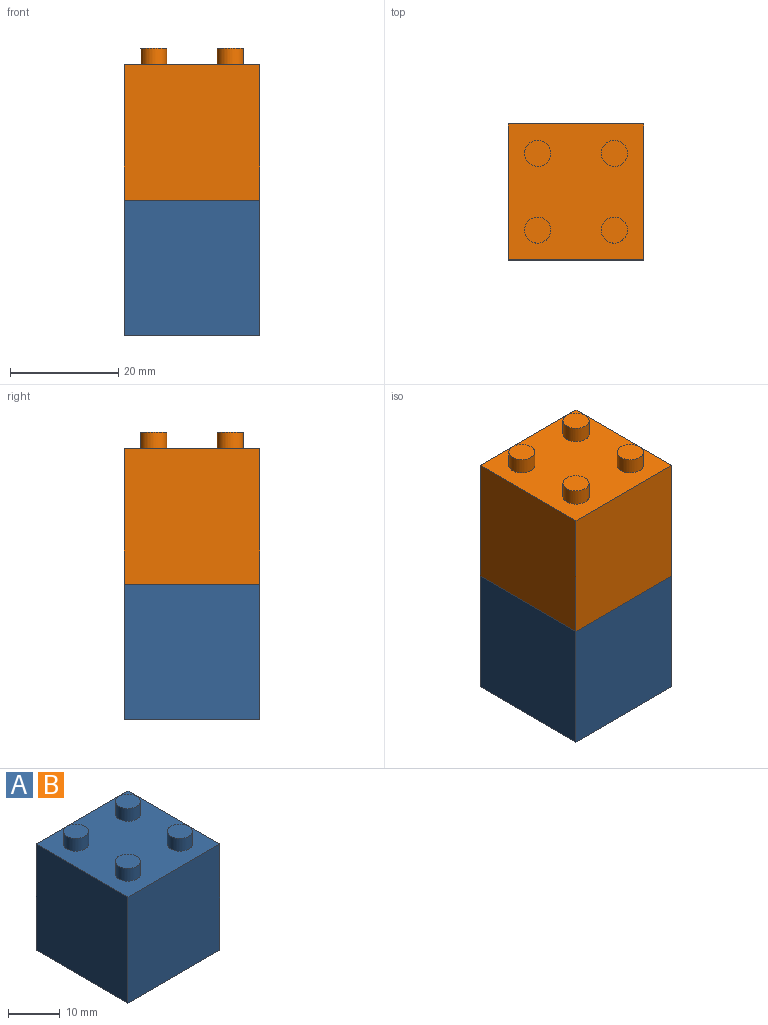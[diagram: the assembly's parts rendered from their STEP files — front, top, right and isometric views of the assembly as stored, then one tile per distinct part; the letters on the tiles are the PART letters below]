
ASSEMBLY  parts=2 mates=1
PART A: 23 faces, bbox 25x25x28 mm
  f0: plane 25x25mm, normal (0,0,-1), area 264mm2, adj f1,f2,f3,f4,f14,f15,f16,f17
  f1: plane 25x25mm, normal (1,0,0), area 625mm2, adj f0,f2,f4,f5
  f2: plane 25x25mm, normal (0,1,0), area 625mm2, adj f0,f1,f3,f5
  f3: plane 25x25mm, normal (-1,0,0), area 625mm2, adj f0,f2,f4,f5
  f4: plane 25x25mm, normal (0,-1,0), area 625mm2, adj f0,f1,f3,f5
  f5: plane 25x25mm, normal (0,0,1), area 552mm2, adj f1,f2,f3,f4,f6,f8,f10,f12
  f6: cylinder r=2.41mm len=4.82mm, axis (0,0,-1), area 45.4mm2, adj f5,f7
  f7: plane 4.82x4.82mm, normal (0,0,1), area 18.3mm2, adj f6
  f8: cylinder r=2.41mm len=4.82mm, axis (0,0,-1), area 45.4mm2, adj f5,f9
  f9: plane 4.82x4.82mm, normal (0,0,1), area 18.3mm2, adj f8
  f10: cylinder r=2.41mm len=4.82mm, axis (0,0,-1), area 45.4mm2, adj f5,f11
  f11: plane 4.82x4.82mm, normal (0,0,1), area 18.3mm2, adj f10
  f12: cylinder r=2.41mm len=4.82mm, axis (0,0,-1), area 45.4mm2, adj f5,f13
  f13: plane 4.82x4.82mm, normal (0,0,1), area 18.3mm2, adj f12
  f14: plane 22x19mm, normal (-1,0,0), area 418mm2, adj f0,f15,f17,f18
  f15: plane 22x19mm, normal (0,-1,0), area 418mm2, adj f0,f14,f16,f18
  f16: plane 22x19mm, normal (1,0,0), area 418mm2, adj f0,f15,f17,f18
  f17: plane 22x19mm, normal (0,1,0), area 418mm2, adj f0,f14,f16,f18
  f18: plane 19x19mm, normal (0,0,-1), area 210.2mm2, adj f14,f15,f16,f17,f19
  f19: cylinder r=6.93mm len=21mm, axis (0,0,1), area 914mm2, adj f18,f20
  f20: plane 13.85x13.85mm, normal (0,0,-1), area 89.2mm2, adj f19,f21
  f21: cylinder r=4.43mm len=21.5mm, axis (0,0,1), area 598.1mm2, adj f20,f22
  f22: plane 8.85x8.85mm, normal (0,0,-1), area 61.6mm2, adj f21
PART B: same geometry as A
PLACE A t=(-26.7,-3.65,-4.28)mm
PLACE B t=(-26.7,-3.65,20.72)mm
MATE planar B.f0 <-> A.f5  axis (0,0,-1) through (-26.7,-16.15,20.72)mm
